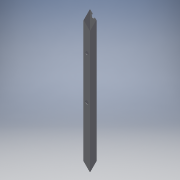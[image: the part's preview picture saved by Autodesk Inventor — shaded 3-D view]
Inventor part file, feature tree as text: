
AUTODESK INVENTOR PART (.ipt)
format: ipt  version: 2016 (Build 200138000, 138)  size: 121,344 bytes
history: native  units: in
note: dims shown in document units (in); Inventor stores cm internally (conversion verified against a paired STEP export)
features: extrude x4, sketch x4
ambient origin geometry x8: Origin, YZ Plane, XZ Plane, XY Plane, X Axis, Y Axis, Z Axis, Center Point
bodies: Solid1 (feature_tree)
feature tree (8):
  extrude  "Extrusion1"  Depth=1.0in
  extrude  "Extrusion2"  Depth=20.0in TaperAngle=0.0deg
  extrude  "Extrusion4"  Depth=0.8in
  extrude  "Extrusion5"  Depth=1.0in
  sketch  "Sketch1"  dims[d0=1.0in d1=1.0in]
  sketch  "Sketch2"  dims[d2=0.0625in d3=20.0in d4=0.0in]
  sketch  "Sketch4"  dims[d5=0.5in d6=0.8in]
  sketch  "Sketch5"  dims[d7=1.0in d8=0.0in d14=0.5in d15=0.456in d16=5.0in d17=1.0in d18=0.0in d19=0.5in d20=0.511in d21=8.694in d22=1.0in d23=0.0in]
